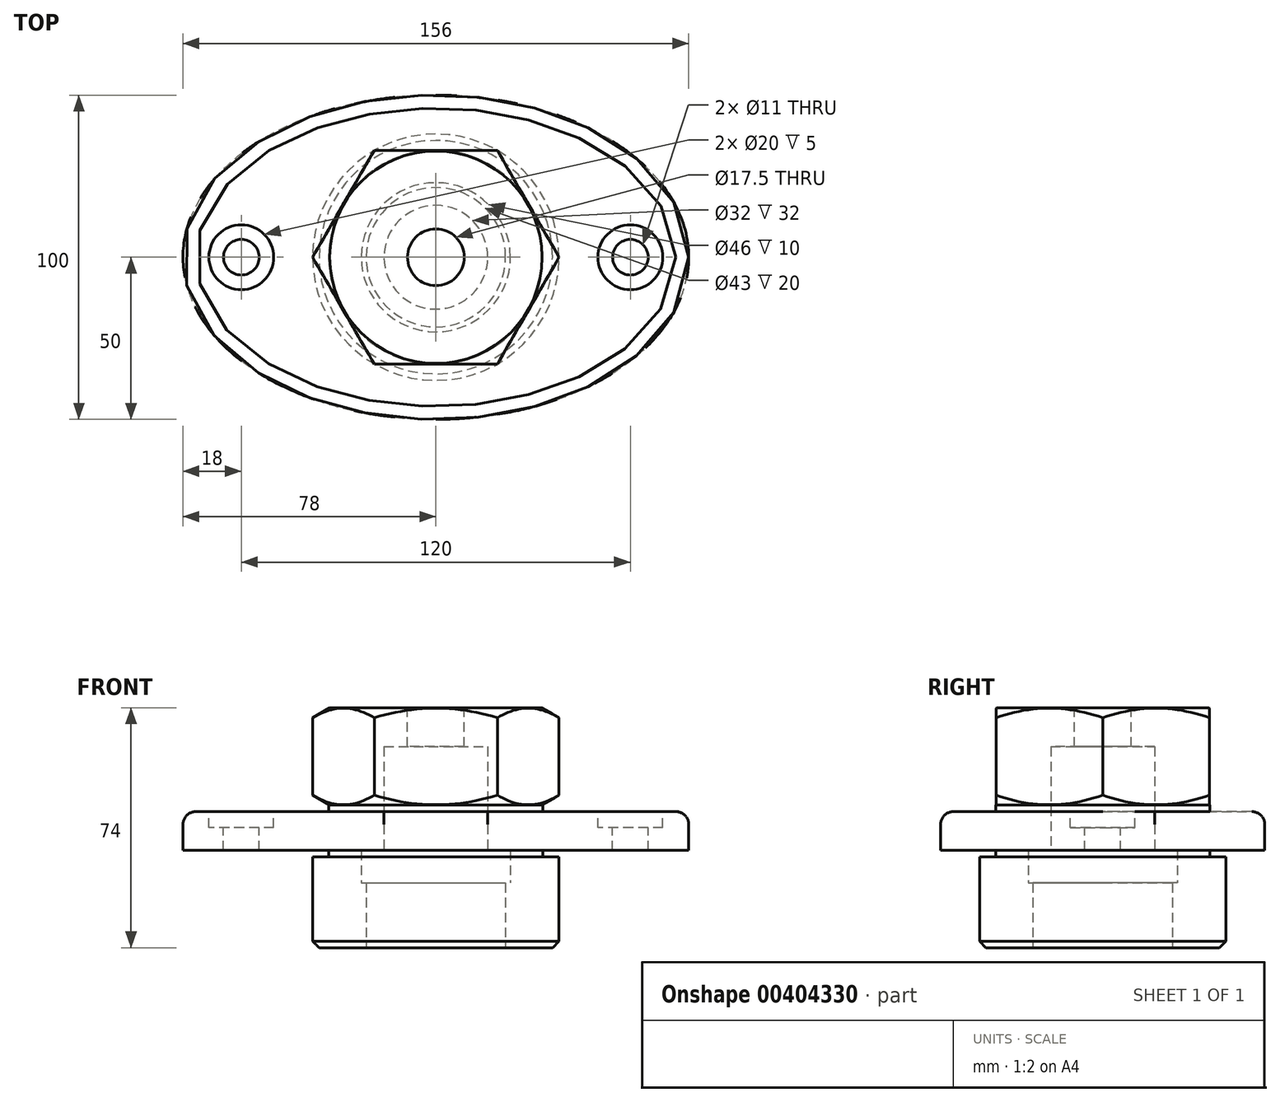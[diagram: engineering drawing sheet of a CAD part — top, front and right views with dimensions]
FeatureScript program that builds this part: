
annotation { "Feature Type Name" : "Feature", "Feature Type Description" : "" }
export const myFeature = defineFeature(function(context is Context, id is Id, definition is map)
    precondition{}
    {
        {
            var Q0;
            Q0=qCreatedBy(makeId("Top.planeOp"),FACE);
            var sketch = newSketch(context, id + "F0", { "sketchPlane" : qUnion([Q0])});
            skEllipse(sketch, "E0", {"center": v(0, 0) * mm, "majorRadius": 78 * mm, "minorRadius": 50 * mm, "majorAxis": v(1, 0)});
            skPoint(sketch, "E1", {"position": v(0, 50) * mm});
            skPoint(sketch, "E2", {"position": v(0, -50) * mm});
            skPoint(sketch, "E3", {"position": v(-78, 0) * mm});
            skPoint(sketch, "E4", {"position": v(78, 0) * mm});
            skSolve(sketch);
        }
        {
            var Q0;
            Q0=makeQuery(id+"F0.imprint","IMPRINT",FACE,{"disambiguationData":[TD([[makeQuery(id+"F0.imprint","IMPRINT",EDGE,{"derivedFrom":sQuery(id+"F0.wireOp",EDGE,"E0")}),1.0]])]});
            extrude(context, id + "F1", {"entities" : qUnion([Q0]), "depth" : 12 * mm});
        }
        {
            var Q0;
            Q0=qCreatedBy(makeId("Front.planeOp"),FACE);
            var sketch = newSketch(context, id + "F2", { "sketchPlane" : qUnion([Q0])});
            skLineSegment(sketch, "E5.top", {"start": v(0, -30) * mm, "end": v(38, -30) * mm});
            skLineSegment(sketch, "E5.right", {"start": v(38, -2) * mm, "end": v(38, -30) * mm});
            skPoint(sketch, "E6", {"position": v(0, -30) * mm});
            skLineSegment(sketch, "E7", {"start": v(0, 0) * mm, "end": v(0, -86.36) * mm, "construction": true});
            skLineSegment(sketch, "E8.top", {"start": v(0, 14) * mm, "end": v(33, 14) * mm});
            skLineSegment(sketch, "E8.right", {"start": v(33, 12) * mm, "end": v(33, 14) * mm});
            skLineSegment(sketch, "E9.trimOffspring", {"start": v(0, 0) * mm, "end": v(0, 92.58) * mm, "construction": true});
            skLineSegment(sketch, "E10.top", {"start": v(38, -2) * mm, "end": v(33, -2) * mm});
            skLineSegment(sketch, "E10.right", {"start": v(33, 0) * mm, "end": v(33, -2) * mm});
            skLineSegment(sketch, "E11", {"start": v(33, 12) * mm, "end": v(0, 12) * mm});
            skLineSegment(sketch, "E12", {"start": v(0, 0) * mm, "end": v(33, 0) * mm});
            skLineSegment(sketch, "E13", {"start": v(0, 14) * mm, "end": v(0, 12) * mm});
            skLineSegment(sketch, "E14", {"start": v(0, 0) * mm, "end": v(0, -30) * mm});
            skSolve(sketch);
        }
        {
            var Q0;
            Q0 = qSketchRegion(id + "F2", true);
            var Q1;
            Q1=sQuery(id+"F2.wireOp",EDGE,"E9.trimOffspring");
            revolve(context, id + "F3", {"operationType" : NewBodyOperationType.ADD, "entities" : qUnion([Q0]), "axis" : qUnion([Q1]), "revolveType" : RevolveType.FULL});
        }
        {
            var Q0;
            Q0=makeQuery(id+"F3.opRevolve","SWEPT_FACE",FACE,{"disambiguationData":[OSD([sQuery(id+"F2.wireOp",EDGE,"E8.top")])]});
            var sketch = newSketch(context, id + "F4", { "sketchPlane" : qUnion([Q0])});
            skCircle(sketch, "E15.cCircle", {"center": v(0, 0) * mm, "radius": 38 * mm, "construction": true});
            skLineSegment(sketch, "E15.0", {"start": v(19, 32.9) * mm, "end": v(38, 0) * mm});
            skLineSegment(sketch, "E15.1", {"start": v(38, 0) * mm, "end": v(19, -32.9) * mm});
            skLineSegment(sketch, "E15.2", {"start": v(19, -32.9) * mm, "end": v(-19, -32.9) * mm});
            skLineSegment(sketch, "E15.3", {"start": v(-19, -32.9) * mm, "end": v(-38, 0) * mm});
            skLineSegment(sketch, "E15.4", {"start": v(-38, 0) * mm, "end": v(-19, 32.9) * mm});
            skLineSegment(sketch, "E15.5", {"start": v(-19, 32.9) * mm, "end": v(19, 32.9) * mm});
            skSolve(sketch);
        }
        {
            var Q0;
            Q0 = qSketchRegion(id + "F4", true);
            extrude(context, id + "F5", {"entities" : qUnion([Q0]), "operationType" : NewBodyOperationType.ADD, "depth" : 30 * mm});
        }
        {
            var Q0;
            Q0=makeQuery(id+"F1.opExtrude","CAP_FACE",FACE,{"disambiguationData":[OSD([sQuery(id+"F0.wireOp",EDGE,"E0")])],"isStart":false});
            var sketch = newSketch(context, id + "F6", { "sketchPlane" : qUnion([Q0])});
            skPoint(sketch, "E16", {"position": v(-60, 0) * mm});
            skPoint(sketch, "E17", {"position": v(60, 0) * mm});
            skLineSegment(sketch, "E18", {"start": v(0, 0) * mm, "end": v(0, -40.5) * mm, "construction": true});
            skSolve(sketch);
        }
        {
            var Q0;
            Q0=sQuery(id+"F6.wireOp",VERTEX,"E16");
            var Q1;
            Q1=sQuery(id+"F6.wireOp",VERTEX,"E17");
            var Q2;
            Q2=makeQuery(id+"F1.opExtrude","SWEPT_BODY",BODY,{"disambiguationData":[OSD([sQuery(id+"F0.wireOp",EDGE,"E0")])]});
            hole(context, id + "F7", {"style" : HoleStyle.C_BORE, "endStyle" : HoleEndStyle.THROUGH, "holeDiameter" : 11 * mm, "cBoreDiameter" : 20 * mm, "cBoreDepth" : 5 * mm, "isTappedThrough" : true, "tappedDepth" : 12 * mm, "tapClearance" : 3, "locations" : qUnion([Q0, Q1]), "scope" : qUnion([Q2])});
        }
        {
            var Q0;
            Q0=qCreatedBy(makeId("Front.planeOp"),FACE);
            var sketch = newSketch(context, id + "F8", { "sketchPlane" : qUnion([Q0])});
            skLineSegment(sketch, "E19.bottom", {"start": v(0, 32) * mm, "end": v(16, 32) * mm});
            skLineSegment(sketch, "E19.right", {"start": v(16, 32) * mm, "end": v(16, 0) * mm});
            skLineSegment(sketch, "E20", {"start": v(0, 54.37) * mm, "end": v(0, 0) * mm, "construction": true});
            skLineSegment(sketch, "E21.bottom", {"start": v(16, 0) * mm, "end": v(23, 0) * mm});
            skLineSegment(sketch, "E21.top", {"start": v(0, -10) * mm, "end": v(23, -10) * mm});
            skLineSegment(sketch, "E21.right", {"start": v(23, 0) * mm, "end": v(23, -10) * mm});
            skLineSegment(sketch, "E22.trimOffspring", {"start": v(0, -10) * mm, "end": v(0, -46.59) * mm, "construction": true});
            skLineSegment(sketch, "E23", {"start": v(0, 32) * mm, "end": v(0, -10) * mm});
            skSolve(sketch);
        }
        {
            var Q0;
            Q0 = qSketchRegion(id + "F8", true);
            var Q1;
            Q1=sQuery(id+"F8.wireOp",EDGE,"E20");
            revolve(context, id + "F9", {"operationType" : NewBodyOperationType.REMOVE, "entities" : qUnion([Q0]), "axis" : qUnion([Q1]), "revolveType" : RevolveType.FULL, "oppositeDirection" : true});
        }
        {
            var Q0;
            Q0=makeQuery(id+"F5.opExtrude","CAP_FACE",FACE,{"disambiguationData":[OSD([sQuery(id+"F4.wireOp",EDGE,"E15.0"),sQuery(id+"F4.wireOp",EDGE,"E15.1"),sQuery(id+"F4.wireOp",EDGE,"E15.2"),sQuery(id+"F4.wireOp",EDGE,"E15.3"),sQuery(id+"F4.wireOp",EDGE,"E15.4"),sQuery(id+"F4.wireOp",EDGE,"E15.5")])],"isStart":false});
            var sketch = newSketch(context, id + "F10", { "sketchPlane" : qUnion([Q0])});
            skPoint(sketch, "E24", {"position": v(0, 0) * mm});
            skSolve(sketch);
        }
        {
            var Q0;
            Q0=sQuery(id+"F10.wireOp",VERTEX,"E24");
            var Q1;
            Q1=makeQuery(id+"F1.opExtrude","SWEPT_BODY",BODY,{"disambiguationData":[OSD([sQuery(id+"F0.wireOp",EDGE,"E0")])]});
            hole(context, id + "F11", {"style" : HoleStyle.SIMPLE, "endStyle" : HoleEndStyle.BLIND, "standardTappedOrClearance" : lookupTablePath({ "standard" : "ISO", "engagement" : "75%", "pitch" : "2.5 mm", "size" : "M20", "type" : "Tapped" }), "standardBlindInLast" : lookupTablePath({ "standard" : "ISO", "engagement" : "75%", "pitch" : "2.5 mm", "size" : "M20", "type" : "Tapped" }), "holeDiameter" : 17.5 * mm, "showTappedDepth" : true, "holeDepth" : 12 * mm, "isTappedThrough" : true, "tappedDepth" : 4.5 * mm, "tapClearance" : 3, "locations" : qUnion([Q0]), "scope" : qUnion([Q1]), "majorDiameter" : 20 * mm});
        }
        {
            var Q0;
            Q0=makeQuery(id+"F3.opRevolve","SWEPT_FACE",FACE,{"disambiguationData":[OSD([sQuery(id+"F2.wireOp",EDGE,"E5.top")])]});
            var sketch = newSketch(context, id + "F12", { "sketchPlane" : qUnion([Q0])});
            skPoint(sketch, "E25", {"position": v(0, 0) * mm});
            skSolve(sketch);
        }
        {
            var Q0;
            Q0=sQuery(id+"F12.wireOp",VERTEX,"E25");
            var Q1;
            Q1=makeQuery(id+"F1.opExtrude","SWEPT_BODY",BODY,{"disambiguationData":[OSD([sQuery(id+"F0.wireOp",EDGE,"E0")])]});
            hole(context, id + "F13", {"style" : HoleStyle.SIMPLE, "endStyle" : HoleEndStyle.BLIND, "holeDiameter" : 43 * mm, "holeDepth" : 20 * mm, "isTappedThrough" : true, "tappedDepth" : 4.5 * mm, "tapClearance" : 3, "locations" : qUnion([Q0]), "scope" : qUnion([Q1])});
        }
        {
            var Q0;
            Q0=makeQuery(id+"F1.opExtrude","CAP_EDGE",EDGE,{"disambiguationData":[OSD([sQuery(id+"F0.wireOp",EDGE,"E0")])],"isStart":false});
            fillet(context, id + "F14", {"entities" : qUnion([Q0]), "radius" : 4 * mm, "tangentPropagation" : true, "allowEdgeOverflow" : false});
        }
        {
            var Q0;
            Q0=makeQuery(id+"F3.opRevolve","SWEPT_EDGE",EDGE,{"disambiguationData":[OSD([sQuery(id+"F2.wireOp",EDGE,"E5.top"),sQuery(id+"F2.wireOp",EDGE,"E5.right")])]});
            chamfer(context, id + "F15", {"entities" : qUnion([Q0]), "chamferType" : ChamferType.OFFSET_ANGLE, "width" : 2 * mm, "oppositeDirection" : false, "angle" : 45 * degree, "tangentPropagation" : true});
        }
        {
            var Q0;
            Q0=qCreatedBy(makeId("Front.planeOp"),FACE);
            var sketch = newSketch(context, id + "F16", { "sketchPlane" : qUnion([Q0])});
            skLineSegment(sketch, "E26", {"start": v(32.75, 44) * mm, "end": v(38, 44) * mm});
            skLineSegment(sketch, "E27", {"start": v(38, 44) * mm, "end": v(38, 40.97) * mm});
            skLineSegment(sketch, "E28", {"start": v(38, 40.97) * mm, "end": v(32.75, 44) * mm});
            skLineSegment(sketch, "E29", {"start": v(38, 29) * mm, "end": v(29.79, 29) * mm, "construction": true});
            skLineSegment(sketch, "E30.MirrorCS", {"start": v(32.75, 14) * mm, "end": v(38, 14) * mm});
            skLineSegment(sketch, "E31.MirrorCS", {"start": v(38, 14) * mm, "end": v(38, 17.03) * mm});
            skLineSegment(sketch, "E32.MirrorCS", {"start": v(38, 17.03) * mm, "end": v(32.75, 14) * mm});
            skLineSegment(sketch, "E33", {"start": v(0, 0) * mm, "end": v(0, 34.08) * mm, "construction": true});
            skSolve(sketch);
        }
        {
            var Q0;
            Q0 = qSketchRegion(id + "F16", true);
            var Q1;
            Q1=sQuery(id+"F16.wireOp",EDGE,"E33");
            revolve(context, id + "F17", {"operationType" : NewBodyOperationType.REMOVE, "entities" : qUnion([Q0]), "axis" : qUnion([Q1]), "revolveType" : RevolveType.FULL, "oppositeDirection" : true});
        }
    });
